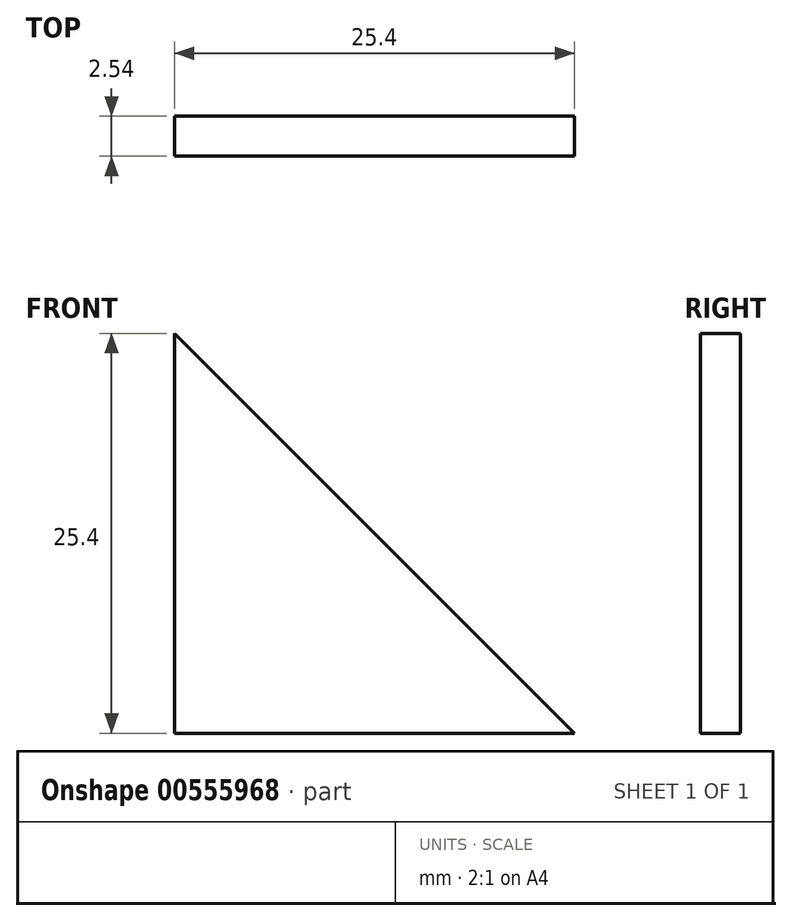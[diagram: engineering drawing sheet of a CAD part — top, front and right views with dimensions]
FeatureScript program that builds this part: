
annotation { "Feature Type Name" : "Feature", "Feature Type Description" : "" }
export const myFeature = defineFeature(function(context is Context, id is Id, definition is map)
    precondition{}
    {
        {
            var Q0;
            Q0=qCreatedBy(makeId("Front.planeOp"),FACE);
            var sketch = newSketch(context, id + "F0", { "sketchPlane" : qUnion([Q0])});
            skLineSegment(sketch, "E0", {"start": v(-51.36, 34.62) * mm, "end": v(-25.96, 34.62) * mm});
            skLineSegment(sketch, "E1", {"start": v(-51.36, 34.62) * mm, "end": v(-51.36, 60.02) * mm});
            skLineSegment(sketch, "E2", {"start": v(-51.36, 60.02) * mm, "end": v(-25.96, 34.62) * mm});
            skSolve(sketch);
        }
        {
            var Q0;
            Q0=makeQuery(id+"F0.imprint","IMPRINT",FACE,{"disambiguationData":[TD([[makeQuery(id+"F0.imprint","IMPRINT",EDGE,{"derivedFrom":sQuery(id+"F0.wireOp",EDGE,"E0")}),1.0]])]});
            extrude(context, id + "F1", {"entities" : qUnion([Q0]), "depth" : 2.54 * mm, "offsetDistance" : 25.4 * mm});
        }
    });
